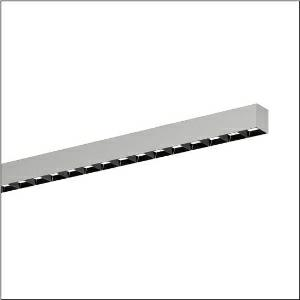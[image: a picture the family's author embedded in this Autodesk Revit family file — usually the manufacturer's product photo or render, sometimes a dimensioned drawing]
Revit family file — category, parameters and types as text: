
# Revit family: silica_r__21_51mx24dc4asb_83d0
name_source: partatom
category: Lighting Fixtures
units: mm (PartAtom-declared; Revit-internal decimal feet)

## family parameters
Cut with Voids When Loaded = No
Host = Face
Light Source = No
Part Type = Normal
Room Calculation Point = No
Round Connector Dimension = Use Diameter
Shared = No

## types (1)
- --- (1 x LED, 10800 lm, 73.7 W, 4000K)
    Apparent Load = 74 VA
    CIE Flux Codes = 74 94 99 100 100
    Color Rendering = 80
    Color Temperature = 4000K
    Default Elevation = 1800 mm
    Description = Silica® 21, office luminaire, primary light control with darklight reflector, of PMMA, black, CAT 2 (L<= 3000cd/m²), light emission: direct distribution, primary light characteristic: asymmetric, installation type: surface-mounted, LED, rated luminous flux: 10.800lm, luminous efficacy: 147lm/W, light colour: 840, colour temperature: 4000K, control gear: DALI 2, with terminal, 3+2-pole, max. 2.5mm², mains connection: 220..240V, AC, 50/60Hz, rated input power: 73.7W, luminaire housing, of aluminium, metallic grey (RAL 9006), length: 3.004mm, width: 53mm, height: 53mm, protection rating (complete): IP20, insulation class (complete): insulation class I (protective earthing), certification: CE, permissible operating ambient temperature: 0..+35°C, standard: EN 50419, packaging unit: 1 piece
    Height = 53 mm
    Lamp = 1 x LED
    Lamp Light Flux = 10800 lm
    Lamp Power = 73.7 W
    Lamp count = 1
    Length = 3004 mm
    Luminous efficacy = 147 lm/W
    Manufacturer = Siteco
    ModVariant = No
    Model = 51MX24DC4ASB
    Mounting Place = Ceiling
    Mounting Type = Surface mounted
    Number of Poles = 1
    OnlyDefault = Yes
    Power Factor = 1
    Product Name = Silica® 21
    Product group = office luminaire | ceiling mounted
    ProductGroupID = 302
    Protection Class = Protection class I
    Protection Degree = IP 20
    RLX_Detail_Level = 1
    RLX_Emergency_Light_Flux = 0 lm
    RLX_Emergency_Type = 0
    RLX_Emergency_Type_DB = No
    RlxData = <blob elided: 63493 chars, md5=74d20925>
    Socket = socket
    Standby Power = 0 W
    System Light Flux = 10800 lm
    System Power = 74 W
    Type Comments = factory setting: luminous flux: 100 % | dim-lin: 254 | 418 mA
    Type Image = l_1335929.jpg
    URL = http://relux.com
    VarID = @adj_122614
    Voltage = 0 V
    Weight = 0.00 kg
    Width = 53 mm

## geometry (parser evidence)
native form markers: Blend x4, Sweep x10
no freeform markers — native parametric forms only
